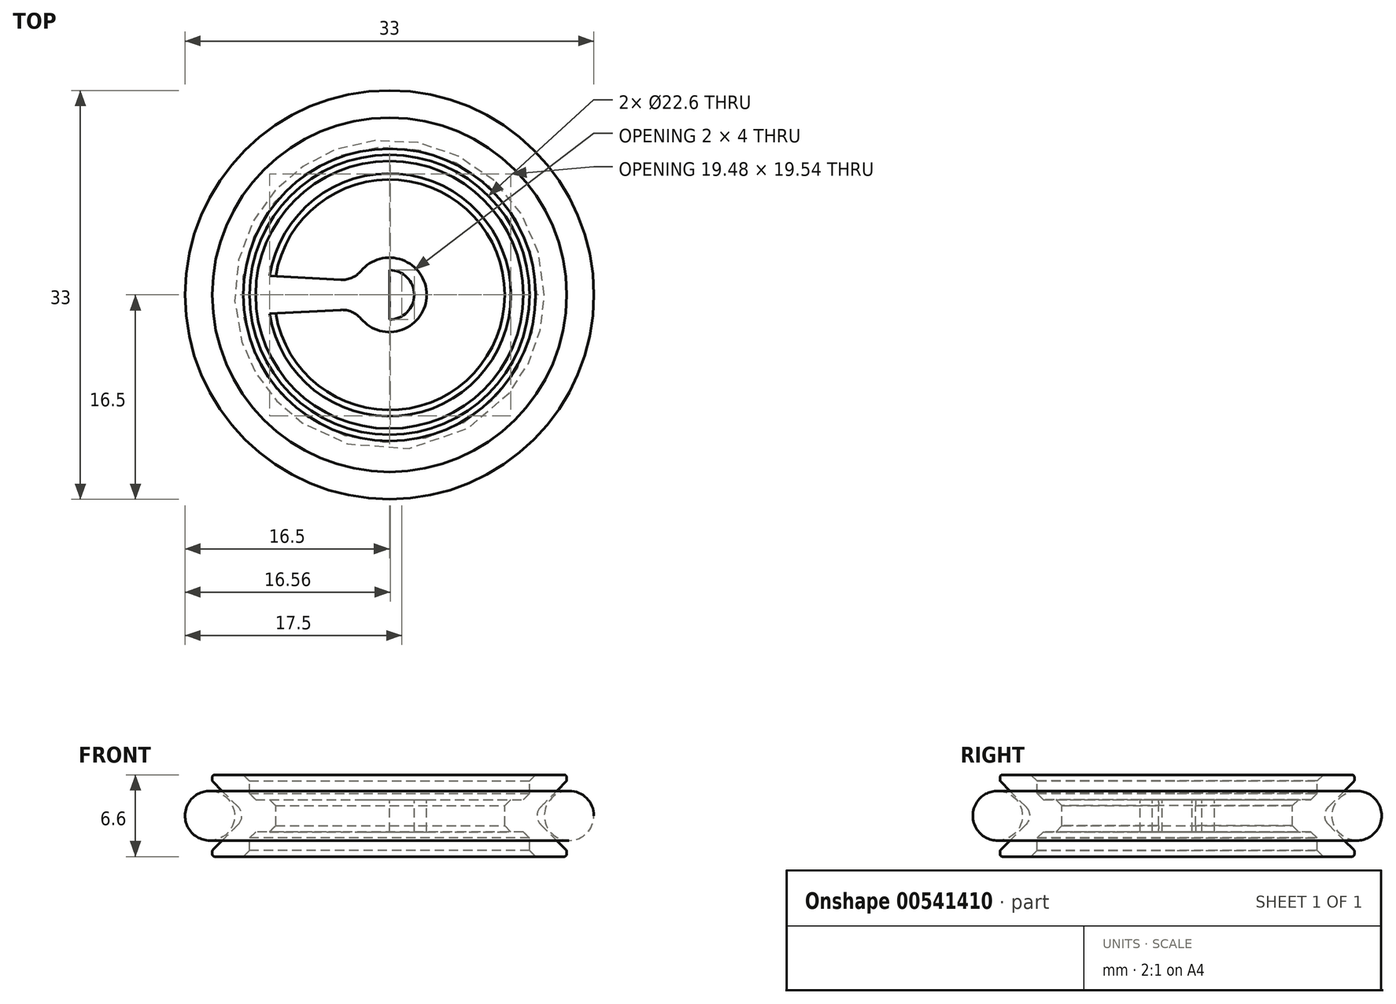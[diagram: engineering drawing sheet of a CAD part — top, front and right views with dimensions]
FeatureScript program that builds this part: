
annotation { "Feature Type Name" : "Feature", "Feature Type Description" : "" }
export const myFeature = defineFeature(function(context is Context, id is Id, definition is map)
    precondition{}
    {
        {
            var Q0;
            Q0=qCreatedBy(makeId("Front.planeOp"),FACE);
            var sketch = newSketch(context, id + "F0", { "sketchPlane" : qUnion([Q0])});
            skLineSegment(sketch, "E0", {"start": v(-14.3, 3.3) * mm, "end": v(-11.3, 3.3) * mm});
            skLineSegment(sketch, "E1", {"start": v(-11.3, 3.3) * mm, "end": v(-11.3, 1.3) * mm});
            skLineSegment(sketch, "E2", {"start": v(-11.3, 1.3) * mm, "end": v(-9.3, 1.3) * mm});
            skLineSegment(sketch, "E3", {"start": v(-9.3, 1.3) * mm, "end": v(-9.3, -1.3) * mm});
            skLineSegment(sketch, "E4", {"start": v(-9.3, -1.3) * mm, "end": v(-11.3, -1.3) * mm});
            skLineSegment(sketch, "E5", {"start": v(-11.3, -1.3) * mm, "end": v(-11.3, -3.3) * mm});
            skLineSegment(sketch, "E6", {"start": v(-11.3, -3.3) * mm, "end": v(-14.3, -3.3) * mm});
            skLineSegment(sketch, "E7", {"start": v(0, 0) * mm, "end": v(-16.3, 0) * mm, "construction": true});
            skLineSegment(sketch, "E8", {"start": v(-14.3, 3.3) * mm, "end": v(-14.3, -3.3) * mm, "construction": true});
            skLineSegment(sketch, "E9", {"start": v(0, 10.44) * mm, "end": v(0, -9.58) * mm, "construction": true});
            skLineSegment(sketch, "E10", {"start": v(-14.3, 3.3) * mm, "end": v(-14.3, 2.8) * mm});
            skLineSegment(sketch, "E11", {"start": v(-14.3, -3.3) * mm, "end": v(-14.3, -2.8) * mm});
            skLineSegment(sketch, "E12", {"start": v(-14.3, 2.8) * mm, "end": v(-11.5, 0) * mm});
            skLineSegment(sketch, "E13", {"start": v(-11.5, 0) * mm, "end": v(-14.3, -2.8) * mm});
            skSolve(sketch);
        }
        {
            var Q0;
            Q0=makeQuery(id+"F0.imprint","IMPRINT",FACE,{"disambiguationData":[TD([[makeQuery(id+"F0.imprint","IMPRINT",EDGE,{"derivedFrom":sQuery(id+"F0.wireOp",EDGE,"E0")}),-1.0]])]});
            var Q1;
            Q1=sQuery(id+"F0.wireOp",EDGE,"E9");
            revolve(context, id + "F1", {"entities" : qUnion([Q0]), "axis" : qUnion([Q1]), "revolveType" : RevolveType.FULL});
        }
        {
            var Q0;
            Q0=makeQuery(id+"F1.opRevolve","SWEPT_FACE",FACE,{"disambiguationData":[OSD([sQuery(id+"F0.wireOp",EDGE,"E2")])]});
            var sketch = newSketch(context, id + "F2", { "sketchPlane" : qUnion([Q0])});
            skLineSegment(sketch, "E14", {"start": v(-9.18, 1.5) * mm, "end": v(0, 1) * mm});
            skLineSegment(sketch, "E15", {"start": v(0, 1) * mm, "end": v(0, -1) * mm});
            skLineSegment(sketch, "E16", {"start": v(0, -1) * mm, "end": v(-9.18, -1.5) * mm});
            skLineSegment(sketch, "E17", {"start": v(0, 0) * mm, "end": v(-10.48, 0) * mm, "construction": true});
            skSolve(sketch);
        }
        {
            var Q0;
            {var subQ0=sQuery(id+"F2.wireOp",EDGE,"E14");Q0=makeQuery(id+"F2.imprint","IMPRINT",FACE,{"disambiguationData":[TD([[makeQuery(id+"F2.imprint","IMPRINT",EDGE,{"derivedFrom":subQ0}),-1.0]])]});}
            var Q1;
            Q1=makeQuery(id+"F1.opRevolve","SWEPT_FACE",FACE,{"disambiguationData":[OSD([sQuery(id+"F0.wireOp",EDGE,"E4")])]});
            extrude(context, id + "F3", {"entities" : qUnion([Q0]), "operationType" : NewBodyOperationType.ADD, "endBound" : BoundingType.UP_TO_SURFACE, "oppositeDirection" : true, "depth" : 25 * mm, "endBoundEntityFace" : qUnion([Q1]), "offsetDistance" : 25 * mm});
        }
        {
            var Q0;
            {var subQ0=sQuery(id+"F2.wireOp",EDGE,"E16");var subQ1=sQuery(id+"F2.wireOp",EDGE,"E15");var subQ2=sQuery(id+"F2.wireOp",EDGE,"E14");var subQ3=sQuery(id+"F0.wireOp",EDGE,"E3");var subQ4=sQuery(id+"F0.wireOp",EDGE,"E2");Q0=makeQuery(id+"F0MuYFyz6MMP7Sl_1.2.F3.boolean.opBoolean","MERGE",FACE,{"derivedFrom":[makeQuery(id+"F0MuYFyz6MMP7Sl_1.1.F3.boolean.opBoolean","MERGE",FACE,{"derivedFrom":[makeQuery(id+"F3.boolean.opBoolean","MERGE",FACE,{"derivedFrom":[makeQuery(id+"F1.opRevolve","SWEPT_FACE",FACE,{"disambiguationData":[OSD([subQ4])]}),makeQuery(id+"F3.opExtrude","CAP_FACE",FACE,{"disambiguationData":[OSD([subQ4,subQ3,subQ2,subQ1,subQ0])],"isStart":true})]}),makeQuery(id+"F0MuYFyz6MMP7Sl_1.1.F3.opExtrude","CAP_FACE",FACE,{"disambiguationData":[OSD([subQ4,subQ3,subQ2,subQ1,subQ0])],"isStart":true})]}),makeQuery(id+"F0MuYFyz6MMP7Sl_1.2.F3.opExtrude","CAP_FACE",FACE,{"disambiguationData":[OSD([subQ4,subQ3,subQ2,subQ1,subQ0])],"isStart":true})]});}
            var sketch = newSketch(context, id + "F4", { "sketchPlane" : qUnion([Q0])});
            skCircle(sketch, "E18", {"center": v(0, 0) * mm, "radius": 3 * mm});
            skLineSegment(sketch, "E19", {"start": v(2.86, 0.92) * mm, "end": v(1.35, 0.92) * mm});
            skLineSegment(sketch, "E20", {"start": v(2.79, -1.11) * mm, "end": v(1.17, -1.11) * mm});
            skLineSegment(sketch, "E21", {"start": v(0, 1.29) * mm, "end": v(0, -1.38) * mm});
            skArc(sketch, "E22", {"start": v(0, 1.29) * mm, "mid": v(0.7, 1.2) * mm, "end": v(1.35, 0.92) * mm});
            skArc(sketch, "E23", {"start": v(0, -1.38) * mm, "mid": v(0.6, -1.31) * mm, "end": v(1.17, -1.11) * mm});
            skSolve(sketch);
        }
        {
            var Q0;
            Q0=qSketchRegion(id+"F4",true);
            var Q1;
            {var subQ0=sQuery(id+"F0.wireOp",EDGE,"E4");Q1=makeQuery(id+"F0MuYFyz6MMP7Sl_1.2.F3.boolean.opBoolean","MERGE",FACE,{"derivedFrom":[makeQuery(id+"F0MuYFyz6MMP7Sl_1.1.F3.boolean.opBoolean","MERGE",FACE,{"derivedFrom":[makeQuery(id+"F3.boolean.opBoolean","MERGE",FACE,{"derivedFrom":[makeQuery(id+"F1.opRevolve","SWEPT_FACE",FACE,{"disambiguationData":[OSD([subQ0])]}),makeQuery(id+"F3.opExtrude","CAP_FACE",FACE,{"disambiguationData":[OSD([subQ0])],"isStart":false})]}),makeQuery(id+"F0MuYFyz6MMP7Sl_1.1.F3.opExtrude","CAP_FACE",FACE,{"disambiguationData":[OSD([subQ0])],"isStart":false})]}),makeQuery(id+"F0MuYFyz6MMP7Sl_1.2.F3.opExtrude","CAP_FACE",FACE,{"disambiguationData":[OSD([subQ0])],"isStart":false})]});}
            extrude(context, id + "F5", {"entities" : qUnion([Q0]), "operationType" : NewBodyOperationType.ADD, "endBound" : BoundingType.UP_TO_SURFACE, "oppositeDirection" : true, "depth" : 25 * mm, "endBoundEntityFace" : qUnion([Q1]), "offsetDistance" : 25 * mm});
        }
        {
            var Q0;
            Q0=makeQuery(id+"F3.opExtrude","SWEPT_EDGE",EDGE,{"disambiguationData":[OSD([sQuery(id+"F0.wireOp",EDGE,"E2"),sQuery(id+"F0.wireOp",EDGE,"E3"),sQuery(id+"F2.wireOp",EDGE,"E14")])]});
            var Q1;
            Q1=makeQuery(id+"F5.boolean.opBoolean","INTERSECT",EDGE,{"derivedFrom":[makeQuery(id+"F3.opExtrude","SWEPT_FACE",FACE,{"disambiguationData":[OSD([sQuery(id+"F2.wireOp",EDGE,"E14")])]}),makeQuery(id+"F5.opExtrude","SWEPT_FACE",FACE,{"disambiguationData":[OSD([sQuery(id+"F4.wireOp",EDGE,"E18")])]})]});
            var Q2;
            Q2=makeQuery(id+"F5.boolean.opBoolean","INTERSECT",EDGE,{"derivedFrom":[makeQuery(id+"F0MuYFyz6MMP7Sl_1.2.F3.opExtrude","SWEPT_FACE",FACE,{"disambiguationData":[OSD([sQuery(id+"F2.wireOp",EDGE,"E16")])]}),makeQuery(id+"F5.opExtrude","SWEPT_FACE",FACE,{"disambiguationData":[OSD([sQuery(id+"F4.wireOp",EDGE,"E18")])]})]});
            var Q3;
            Q3=makeQuery(id+"F0MuYFyz6MMP7Sl_1.2.F3.opExtrude","SWEPT_EDGE",EDGE,{"disambiguationData":[OSD([sQuery(id+"F0.wireOp",EDGE,"E2"),sQuery(id+"F0.wireOp",EDGE,"E3"),sQuery(id+"F2.wireOp",EDGE,"E16")])]});
            var Q4;
            Q4=makeQuery(id+"F0MuYFyz6MMP7Sl_1.2.F3.opExtrude","SWEPT_EDGE",EDGE,{"disambiguationData":[OSD([sQuery(id+"F0.wireOp",EDGE,"E2"),sQuery(id+"F0.wireOp",EDGE,"E3"),sQuery(id+"F2.wireOp",EDGE,"E14")])]});
            var Q5;
            Q5=makeQuery(id+"F5.boolean.opBoolean","INTERSECT",EDGE,{"derivedFrom":[makeQuery(id+"F0MuYFyz6MMP7Sl_1.2.F3.opExtrude","SWEPT_FACE",FACE,{"disambiguationData":[OSD([sQuery(id+"F2.wireOp",EDGE,"E14")])]}),makeQuery(id+"F5.opExtrude","SWEPT_FACE",FACE,{"disambiguationData":[OSD([sQuery(id+"F4.wireOp",EDGE,"E18")])]})]});
            var Q6;
            Q6=makeQuery(id+"F5.boolean.opBoolean","INTERSECT",EDGE,{"derivedFrom":[makeQuery(id+"F0MuYFyz6MMP7Sl_1.1.F3.opExtrude","SWEPT_FACE",FACE,{"disambiguationData":[OSD([sQuery(id+"F2.wireOp",EDGE,"E16")])]}),makeQuery(id+"F5.opExtrude","SWEPT_FACE",FACE,{"disambiguationData":[OSD([sQuery(id+"F4.wireOp",EDGE,"E18")])]})]});
            var Q7;
            Q7=makeQuery(id+"F0MuYFyz6MMP7Sl_1.1.F3.opExtrude","SWEPT_EDGE",EDGE,{"disambiguationData":[OSD([sQuery(id+"F0.wireOp",EDGE,"E2"),sQuery(id+"F0.wireOp",EDGE,"E3"),sQuery(id+"F2.wireOp",EDGE,"E16")])]});
            var Q8;
            Q8=makeQuery(id+"F5.boolean.opBoolean","INTERSECT",EDGE,{"derivedFrom":[makeQuery(id+"F0MuYFyz6MMP7Sl_1.1.F3.opExtrude","SWEPT_FACE",FACE,{"disambiguationData":[OSD([sQuery(id+"F2.wireOp",EDGE,"E14")])]}),makeQuery(id+"F5.opExtrude","SWEPT_FACE",FACE,{"disambiguationData":[OSD([sQuery(id+"F4.wireOp",EDGE,"E18")])]})]});
            var Q9;
            Q9=makeQuery(id+"F5.boolean.opBoolean","INTERSECT",EDGE,{"derivedFrom":[makeQuery(id+"F3.opExtrude","SWEPT_FACE",FACE,{"disambiguationData":[OSD([sQuery(id+"F2.wireOp",EDGE,"E16")])]}),makeQuery(id+"F5.opExtrude","SWEPT_FACE",FACE,{"disambiguationData":[OSD([sQuery(id+"F4.wireOp",EDGE,"E18")])]})]});
            var Q10;
            Q10=makeQuery(id+"F0MuYFyz6MMP7Sl_1.1.F3.opExtrude","SWEPT_EDGE",EDGE,{"disambiguationData":[OSD([sQuery(id+"F0.wireOp",EDGE,"E2"),sQuery(id+"F0.wireOp",EDGE,"E3"),sQuery(id+"F2.wireOp",EDGE,"E14")])]});
            var Q11;
            Q11=makeQuery(id+"F3.opExtrude","SWEPT_EDGE",EDGE,{"disambiguationData":[OSD([sQuery(id+"F0.wireOp",EDGE,"E2"),sQuery(id+"F0.wireOp",EDGE,"E3"),sQuery(id+"F2.wireOp",EDGE,"E16")])]});
            fillet(context, id + "F6", {"entities" : qUnion([Q0, Q1, Q2, Q3, Q4, Q5, Q6, Q7, Q8, Q9, Q10, Q11]), "radius" : 2 * mm, "tangentPropagation" : true, "allowEdgeOverflow" : false});
        }
        {
            var Q0;
            {var subQ0=sQuery(id+"F2.wireOp",EDGE,"E16");var subQ1=sQuery(id+"F2.wireOp",EDGE,"E15");var subQ2=sQuery(id+"F2.wireOp",EDGE,"E14");var subQ3=sQuery(id+"F0.wireOp",EDGE,"E3");var subQ4=sQuery(id+"F0.wireOp",EDGE,"E2");Q0=makeQuery(id+"F5.boolean.opBoolean","MERGE",FACE,{"derivedFrom":[makeQuery(id+"F0MuYFyz6MMP7Sl_1.2.F3.boolean.opBoolean","MERGE",FACE,{"derivedFrom":[makeQuery(id+"F0MuYFyz6MMP7Sl_1.1.F3.boolean.opBoolean","MERGE",FACE,{"derivedFrom":[makeQuery(id+"F3.boolean.opBoolean","MERGE",FACE,{"derivedFrom":[makeQuery(id+"F1.opRevolve","SWEPT_FACE",FACE,{"disambiguationData":[OSD([subQ4])]}),makeQuery(id+"F3.opExtrude","CAP_FACE",FACE,{"disambiguationData":[OSD([subQ4,subQ3,subQ2,subQ1,subQ0])],"isStart":true})]}),makeQuery(id+"F0MuYFyz6MMP7Sl_1.1.F3.opExtrude","CAP_FACE",FACE,{"disambiguationData":[OSD([subQ4,subQ3,subQ2,subQ1,subQ0])],"isStart":true})]}),makeQuery(id+"F0MuYFyz6MMP7Sl_1.2.F3.opExtrude","CAP_FACE",FACE,{"disambiguationData":[OSD([subQ4,subQ3,subQ2,subQ1,subQ0])],"isStart":true})]}),makeQuery(id+"F5.opExtrude","CAP_FACE",FACE,{"disambiguationData":[OSD([sQuery(id+"F4.wireOp",EDGE,"E18")])],"isStart":true})]});}
            var sketch = newSketch(context, id + "F7", { "sketchPlane" : qUnion([Q0])});
            skArc(sketch, "E24", {"start": v(0, 2) * mm, "mid": v(2, 0) * mm, "end": v(0, -2) * mm});
            skLineSegment(sketch, "E25", {"start": v(0, 2) * mm, "end": v(0, -2) * mm});
            skLineSegment(sketch, "E26", {"start": v(1.73, 1) * mm, "end": v(5, 1) * mm});
            skLineSegment(sketch, "E27", {"start": v(5, 1) * mm, "end": v(5, -1) * mm});
            skLineSegment(sketch, "E28", {"start": v(5, -1) * mm, "end": v(1.73, -1) * mm});
            skLineSegment(sketch, "E29", {"start": v(0, 0) * mm, "end": v(5, 0) * mm, "construction": true});
            skSolve(sketch);
        }
        {
            var Q0;
            {var subQ0=sQuery(id+"F7.wireOp",EDGE,"E25");Q0=makeQuery(id+"F7.imprint","IMPRINT",FACE,{"disambiguationData":[TD([[makeQuery(id+"F7.imprint","IMPRINT",EDGE,{"derivedFrom":subQ0}),1.0]])]});}
            var Q1;
            {var subQ18=sQuery(id+"F7.wireOp",EDGE,"E27");Q1=makeQuery(id+"F7.imprint","IMPRINT",FACE,{"disambiguationData":[TD([[makeQuery(id+"F7.imprint","IMPRINT",EDGE,{"derivedFrom":subQ18}),-1.0]])]});}
            var Q2;
            {var subQ0=sQuery(id+"F7.wireOp",EDGE,"E26");var subQ1=sQuery(id+"F7.wireOp",EDGE,"E24");var subQ2=makeQuery(id+"F7.imprint","INTERSECT",VERTEX,{"derivedFrom":[subQ1,subQ0]});Q2=makeQuery(id+"F7.imprint","IMPRINT",FACE,{"disambiguationData":[TD([[makeQuery(id+"F7.imprint","IMPRINT",EDGE,{"disambiguationData":[TD([[subQ2,-1.0]])],"derivedFrom":subQ1}),1.0]])]});}
            var Q3;
            {var subQ0=sQuery(id+"F4.wireOp",EDGE,"E18");var subQ1=makeQuery(id+"F5.opExtrude","CAP_FACE",FACE,{"disambiguationData":[OSD([subQ0])],"isStart":true});var subQ2=sQuery(id+"F2.wireOp",EDGE,"E16");var subQ3=sQuery(id+"F2.wireOp",EDGE,"E15");var subQ4=sQuery(id+"F2.wireOp",EDGE,"E14");var subQ5=sQuery(id+"F0.wireOp",EDGE,"E3");var subQ6=sQuery(id+"F0.wireOp",EDGE,"E2");var subQ7=makeQuery(id+"F0MuYFyz6MMP7Sl_1.2.F3.opExtrude","CAP_FACE",FACE,{"disambiguationData":[OSD([subQ6,subQ5,subQ4,subQ3,subQ2])],"isStart":true});var subQ8=makeQuery(id+"F0MuYFyz6MMP7Sl_1.1.F3.opExtrude","CAP_FACE",FACE,{"disambiguationData":[OSD([subQ6,subQ5,subQ4,subQ3,subQ2])],"isStart":true});var subQ9=makeQuery(id+"F3.opExtrude","CAP_FACE",FACE,{"disambiguationData":[OSD([subQ6,subQ5,subQ4,subQ3,subQ2])],"isStart":true});var subQ10=makeQuery(id+"F1.opRevolve","SWEPT_FACE",FACE,{"disambiguationData":[OSD([subQ6])]});var subQ11=makeQuery(id+"F5.boolean.opBoolean","MERGE",FACE,{"derivedFrom":[makeQuery(id+"F0MuYFyz6MMP7Sl_1.2.F3.boolean.opBoolean","MERGE",FACE,{"derivedFrom":[makeQuery(id+"F0MuYFyz6MMP7Sl_1.1.F3.boolean.opBoolean","MERGE",FACE,{"derivedFrom":[makeQuery(id+"F3.boolean.opBoolean","MERGE",FACE,{"derivedFrom":[subQ10,subQ9]}),subQ8]}),subQ7]}),subQ1]});var subQ12=subQ11;Q3=makeQuery(id+"F7.imprint","IMPRINT",FACE,{"disambiguationData":[TD([[makeQuery(id+"F7.imprint","IMPRINT",EDGE,{"derivedFrom":makeQuery(id+"F9.opChamfer","BLEND_EDGE",EDGE,{"blendedFrom":[makeQuery(id+"F3.opExtrude","CAP_EDGE",EDGE,{"disambiguationData":[OSD([subQ2])],"isStart":true}),subQ12],"blendedInto":[subQ12]})}),-1.0]])]});}
            extrude(context, id + "F8", {"entities" : qUnion([Q0, Q1, Q2, Q3]), "operationType" : NewBodyOperationType.REMOVE, "endBound" : BoundingType.THROUGH_ALL, "oppositeDirection" : true, "depth" : 25 * mm, "offsetDistance" : 25 * mm});
        }
        {
            var Q0;
            {var subQ0=sQuery(id+"F2.wireOp",EDGE,"E16");var subQ3=sQuery(id+"F0.wireOp",EDGE,"E3");var subQ4=sQuery(id+"F0.wireOp",EDGE,"E2");Q0=makeQuery(id+"F0MuYFyz6MMP7Sl_1.1.F3.boolean.opBoolean","SPLIT",EDGE,{"disambiguationData":[TD([makeQuery(id+"F3.opExtrude","SWEPT_FACE",FACE,{"disambiguationData":[OSD([subQ0])]})])],"derivedFrom":makeQuery(id+"F1.opRevolve","SWEPT_EDGE",EDGE,{"disambiguationData":[OSD([subQ4,subQ3])]})});}
            var Q1;
            {var subQ2=sQuery(id+"F2.wireOp",EDGE,"E14");var subQ3=sQuery(id+"F0.wireOp",EDGE,"E3");var subQ4=sQuery(id+"F0.wireOp",EDGE,"E2");var subQ7=makeQuery(id+"F3.opExtrude","SWEPT_FACE",FACE,{"disambiguationData":[OSD([subQ2])]});Q1=makeQuery(id+"F0MuYFyz6MMP7Sl_1.2.F3.boolean.opBoolean","SPLIT",EDGE,{"disambiguationData":[TD([subQ7])],"derivedFrom":makeQuery(id+"F0MuYFyz6MMP7Sl_1.1.F3.boolean.opBoolean","SPLIT",EDGE,{"disambiguationData":[TD([subQ7])],"derivedFrom":makeQuery(id+"F1.opRevolve","SWEPT_EDGE",EDGE,{"disambiguationData":[OSD([subQ4,subQ3])]})})});}
            var Q2;
            {var subQ0=sQuery(id+"F2.wireOp",EDGE,"E16");var subQ2=sQuery(id+"F2.wireOp",EDGE,"E14");var subQ3=sQuery(id+"F0.wireOp",EDGE,"E3");var subQ4=sQuery(id+"F0.wireOp",EDGE,"E2");var subQ9=makeQuery(id+"F0MuYFyz6MMP7Sl_1.1.F3.opExtrude","SWEPT_FACE",FACE,{"disambiguationData":[OSD([subQ0])]});Q2=makeQuery(id+"F0MuYFyz6MMP7Sl_1.2.F3.boolean.opBoolean","SPLIT",EDGE,{"disambiguationData":[TD([subQ9])],"derivedFrom":makeQuery(id+"F0MuYFyz6MMP7Sl_1.1.F3.boolean.opBoolean","SPLIT",EDGE,{"disambiguationData":[TD([makeQuery(id+"F3.opExtrude","SWEPT_FACE",FACE,{"disambiguationData":[OSD([subQ2])]})])],"derivedFrom":makeQuery(id+"F1.opRevolve","SWEPT_EDGE",EDGE,{"disambiguationData":[OSD([subQ4,subQ3])]})})});}
            var Q3;
            {var subQ0=sQuery(id+"F0.wireOp",EDGE,"E4");var subQ1=sQuery(id+"F0.wireOp",EDGE,"E3");Q3=makeQuery(id+"F0MuYFyz6MMP7Sl_1.1.F3.boolean.opBoolean","SPLIT",EDGE,{"disambiguationData":[TD([makeQuery(id+"F3.opExtrude","SWEPT_FACE",FACE,{"disambiguationData":[OSD([sQuery(id+"F2.wireOp",EDGE,"E16")])]})])],"derivedFrom":makeQuery(id+"F1.opRevolve","SWEPT_EDGE",EDGE,{"disambiguationData":[OSD([subQ1,subQ0])]})});}
            var Q4;
            {var subQ0=makeQuery(id+"F3.opExtrude","SWEPT_FACE",FACE,{"disambiguationData":[OSD([sQuery(id+"F2.wireOp",EDGE,"E14")])]});var subQ1=sQuery(id+"F0.wireOp",EDGE,"E4");var subQ4=sQuery(id+"F0.wireOp",EDGE,"E3");Q4=makeQuery(id+"F0MuYFyz6MMP7Sl_1.2.F3.boolean.opBoolean","SPLIT",EDGE,{"disambiguationData":[TD([subQ0])],"derivedFrom":makeQuery(id+"F0MuYFyz6MMP7Sl_1.1.F3.boolean.opBoolean","SPLIT",EDGE,{"disambiguationData":[TD([subQ0])],"derivedFrom":makeQuery(id+"F1.opRevolve","SWEPT_EDGE",EDGE,{"disambiguationData":[OSD([subQ4,subQ1])]})})});}
            var Q5;
            {var subQ0=sQuery(id+"F0.wireOp",EDGE,"E4");var subQ2=makeQuery(id+"F0MuYFyz6MMP7Sl_1.1.F3.opExtrude","SWEPT_FACE",FACE,{"disambiguationData":[OSD([sQuery(id+"F2.wireOp",EDGE,"E16")])]});var subQ4=sQuery(id+"F0.wireOp",EDGE,"E3");var subQ7=sQuery(id+"F2.wireOp",EDGE,"E14");Q5=makeQuery(id+"F0MuYFyz6MMP7Sl_1.2.F3.boolean.opBoolean","SPLIT",EDGE,{"disambiguationData":[TD([subQ2])],"derivedFrom":makeQuery(id+"F0MuYFyz6MMP7Sl_1.1.F3.boolean.opBoolean","SPLIT",EDGE,{"disambiguationData":[TD([makeQuery(id+"F3.opExtrude","SWEPT_FACE",FACE,{"disambiguationData":[OSD([subQ7])]})])],"derivedFrom":makeQuery(id+"F1.opRevolve","SWEPT_EDGE",EDGE,{"disambiguationData":[OSD([subQ4,subQ0])]})})});}
            var Q6;
            Q6=makeQuery(id+"F1.opRevolve","SWEPT_EDGE",EDGE,{"disambiguationData":[OSD([sQuery(id+"F0.wireOp",EDGE,"E4"),sQuery(id+"F0.wireOp",EDGE,"E5")])]});
            var Q7;
            Q7=makeQuery(id+"F1.opRevolve","SWEPT_EDGE",EDGE,{"disambiguationData":[OSD([sQuery(id+"F0.wireOp",EDGE,"E5"),sQuery(id+"F0.wireOp",EDGE,"E6")])]});
            var Q8;
            Q8=makeQuery(id+"F1.opRevolve","SWEPT_EDGE",EDGE,{"disambiguationData":[OSD([sQuery(id+"F0.wireOp",EDGE,"E1"),sQuery(id+"F0.wireOp",EDGE,"E2")])]});
            var Q9;
            Q9=makeQuery(id+"F1.opRevolve","SWEPT_EDGE",EDGE,{"disambiguationData":[OSD([sQuery(id+"F0.wireOp",EDGE,"E0"),sQuery(id+"F0.wireOp",EDGE,"E1")])]});
            chamfer(context, id + "F9", {"entities" : qUnion([Q0, Q1, Q2, Q3, Q4, Q5, Q6, Q7, Q8, Q9]), "width" : 0.5 * mm, "tangentPropagation" : true});
        }
        {
            var Q0;
            Q0=makeQuery(id+"F1.opRevolve","SWEPT_FACE",FACE,{"disambiguationData":[OSD([sQuery(id+"F0.wireOp",EDGE,"E11")])]});
            var Q1;
            Q1=makeQuery(id+"F1.opRevolve","SWEPT_FACE",FACE,{"disambiguationData":[OSD([sQuery(id+"F0.wireOp",EDGE,"E10")])]});
            fillet(context, id + "F10", {"entities" : qUnion([Q0, Q1]), "radius" : 0.2 * mm, "tangentPropagation" : true, "allowEdgeOverflow" : false});
        }
        {
            var Q0;
            Q0=makeQuery(id+"F1.opRevolve","SWEPT_EDGE",EDGE,{"disambiguationData":[OSD([sQuery(id+"F0.wireOp",EDGE,"E12"),sQuery(id+"F0.wireOp",EDGE,"E13")])]});
            fillet(context, id + "F11", {"entities" : qUnion([Q0]), "radius" : 1 * mm, "tangentPropagation" : true, "allowEdgeOverflow" : false});
        }
        {
            var Q0;
            Q0=qCreatedBy(makeId("Top.planeOp"),FACE);
            var sketch = newSketch(context, id + "F12", { "sketchPlane" : qUnion([Q0])});
            skCircle(sketch, "E30", {"center": v(0, 0) * mm, "radius": 15.85 * mm});
            skSolve(sketch);
        }
        {
            var Q0;
            Q0=qCreatedBy(makeId("Front.planeOp"),FACE);
            var sketch = newSketch(context, id + "F13", { "sketchPlane" : qUnion([Q0])});
            skCircle(sketch, "E31", {"center": v(14.5, 0) * mm, "radius": 2 * mm});
            skSolve(sketch);
        }
        {
            var Q0;
            Q0=makeQuery(id+"F13.imprint","IMPRINT",FACE,{"disambiguationData":[TD([[makeQuery(id+"F13.imprint","IMPRINT",EDGE,{"derivedFrom":sQuery(id+"F13.wireOp",EDGE,"E31")}),1.0]])]});
            var Q1;
            Q1=sQuery(id+"F13.wireOp",EDGE,"E31");
            var Q2;
            Q2=sQuery(id+"F12.wireOp",EDGE,"E30");
            sweep(context, id + "F14", {"profiles" : qUnion([Q0]), "surfaceProfiles" : qUnion([Q1]), "path" : qUnion([Q2])});
        }
    });
